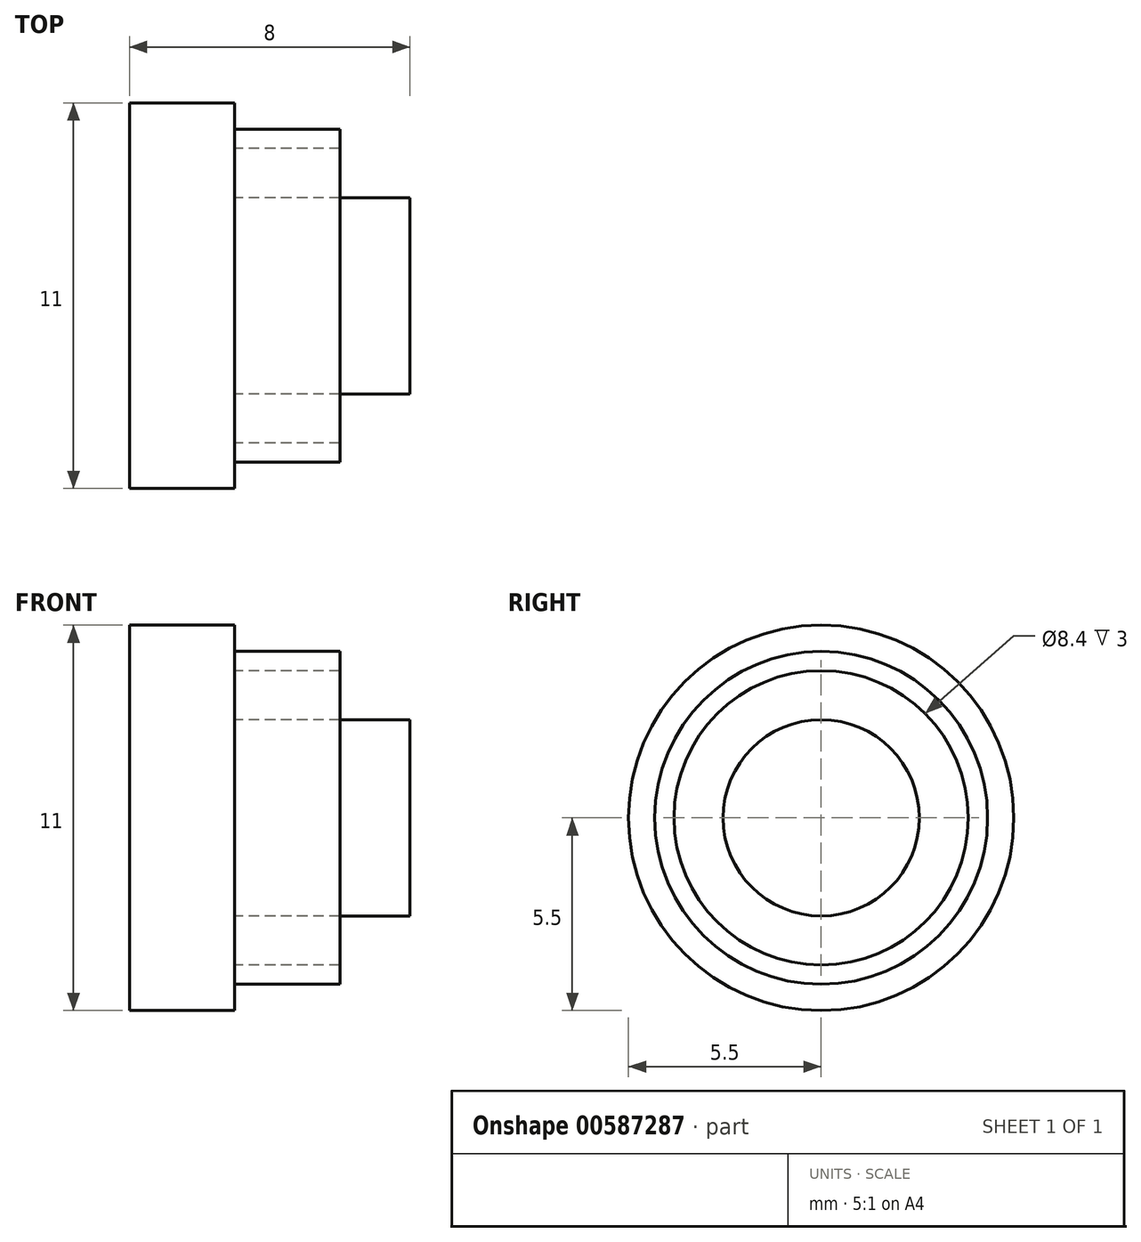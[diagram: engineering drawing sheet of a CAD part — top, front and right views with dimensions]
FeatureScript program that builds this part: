
annotation { "Feature Type Name" : "Feature", "Feature Type Description" : "" }
export const myFeature = defineFeature(function(context is Context, id is Id, definition is map)
    precondition{}
    {
        {
            var Q0;
            Q0=qCreatedBy(makeId("Right.planeOp"),FACE);
            var sketch = newSketch(context, id + "F0", { "sketchPlane" : qUnion([Q0])});
            skCircle(sketch, "E0", {"center": v(0, 0) * mm, "radius": 5.5 * mm});
            skSolve(sketch);
        }
        {
            var Q0;
            Q0 = qSketchRegion(id + "F0", true);
            extrude(context, id + "F1", {"entities" : qUnion([Q0]), "depth" : 3 * mm, "offsetDistance" : 25 * mm});
        }
        {
            var Q0;
            Q0=makeQuery(id+"F1.opExtrude","CAP_FACE",FACE,{"disambiguationData":[OSD([sQuery(id+"F0.wireOp",EDGE,"E0")])],"isStart":false});
            var sketch = newSketch(context, id + "F2", { "sketchPlane" : qUnion([Q0])});
            skCircle(sketch, "E1", {"center": v(0, 0) * mm, "radius": 4.2 * mm});
            skCircle(sketch, "E2", {"center": v(0, 0) * mm, "radius": 2.8 * mm});
            skCircle(sketch, "E3", {"center": v(0, 0) * mm, "radius": 4.75 * mm});
            skSolve(sketch);
        }
        {
            var Q0;
            Q0=makeQuery(id+"F2.imprint","IMPRINT",FACE,{"disambiguationData":[TD([[makeQuery(id+"F2.imprint","IMPRINT",EDGE,{"derivedFrom":sQuery(id+"F2.wireOp",EDGE,"E2")}),1.0]])]});
            extrude(context, id + "F3", {"entities" : qUnion([Q0]), "operationType" : NewBodyOperationType.ADD, "depth" : 5 * mm, "offsetDistance" : 25 * mm});
        }
        {
            var Q0;
            Q0=makeQuery(id+"F2.imprint","IMPRINT",FACE,{"disambiguationData":[TD([[makeQuery(id+"F2.imprint","IMPRINT",EDGE,{"derivedFrom":sQuery(id+"F2.wireOp",EDGE,"E1")}),-1.0]])]});
            extrude(context, id + "F4", {"entities" : qUnion([Q0]), "operationType" : NewBodyOperationType.ADD, "depth" : 3 * mm, "offsetDistance" : 25 * mm});
        }
    });
